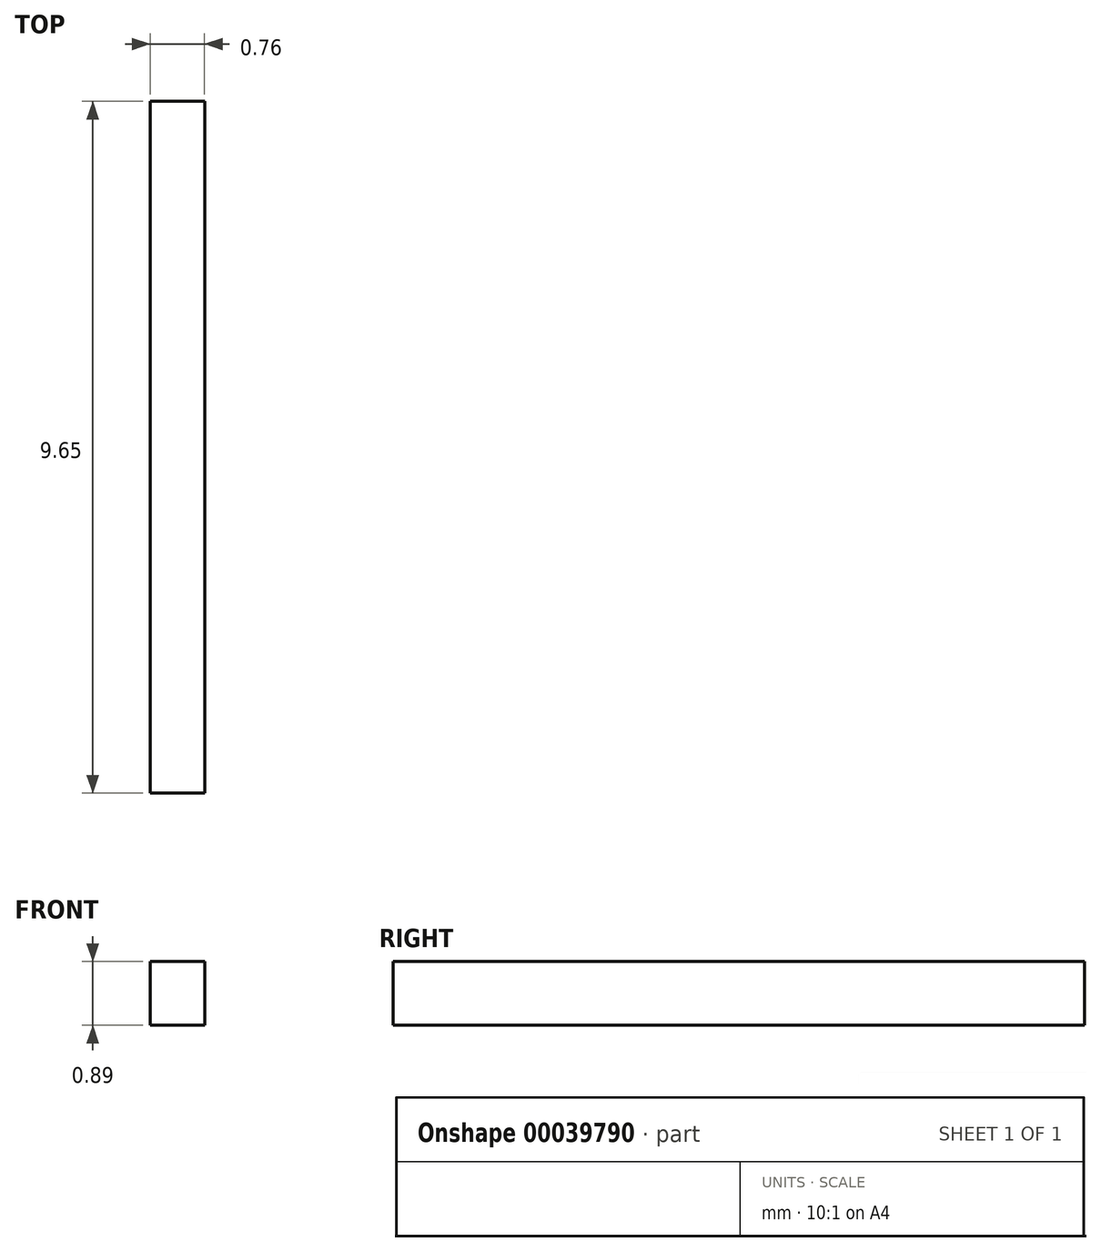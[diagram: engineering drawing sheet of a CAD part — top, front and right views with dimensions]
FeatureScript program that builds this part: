
annotation { "Feature Type Name" : "Feature", "Feature Type Description" : "" }
export const myFeature = defineFeature(function(context is Context, id is Id, definition is map)
    precondition{}
    {
        {
            var Q0;
            Q0=qCreatedBy(makeId("Front.planeOp"),FACE);
            var sketch = newSketch(context, id + "F0", { "sketchPlane" : qUnion([Q0])});
            skLineSegment(sketch, "E0.bottom", {"start": v(0, 0) * mm, "end": v(0.76, 0) * mm});
            skLineSegment(sketch, "E0.top", {"start": v(0, 0.89) * mm, "end": v(0.76, 0.89) * mm});
            skLineSegment(sketch, "E0.left", {"start": v(0, 0) * mm, "end": v(0, 0.89) * mm});
            skLineSegment(sketch, "E0.right", {"start": v(0.76, 0) * mm, "end": v(0.76, 0.89) * mm});
            skSolve(sketch);
        }
        {
            var Q0;
            Q0 = qSketchRegion(id + "F0", true);
            extrude(context, id + "F1", {"entities" : qUnion([Q0]), "depth" : 9.65 * mm});
        }
    });
